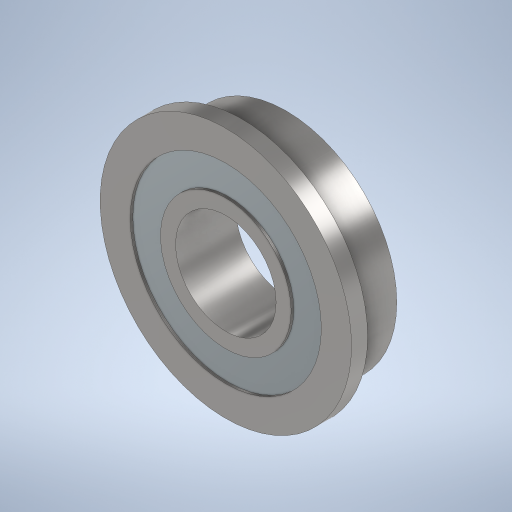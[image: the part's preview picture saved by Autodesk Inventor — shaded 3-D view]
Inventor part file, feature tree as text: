
AUTODESK INVENTOR PART (.ipt)
format: ipt  version: 2024 (Build 280153000, 153)  size: 294,400 bytes
history: native  units: mm
features: extrude x3, sketch x2
ambient origin geometry x8: Origin, YZ Plane, XZ Plane, XY Plane, X Axis, Y Axis, Z Axis, Center Point
bodies: Solid1 (feature_tree)
feature tree (5):
  sketch  "Sketch1"  dims[d0=5.0mm d1=11.0mm]
  extrude  "Extrusion1"  Depth=11.0mm
  extrude  "Extrusion2"  Depth=0.8mm
  extrude  "Extrusion3"  Depth=3.0mm TaperAngle=0.0deg
  sketch  "Sketch2"  dims[d2=0.75mm d3=0.75mm d4=3.0mm d5=0.0mm d6=2.75mm d7=0.0mm d8=12.5mm d9=0.8mm d10=0.0mm]
